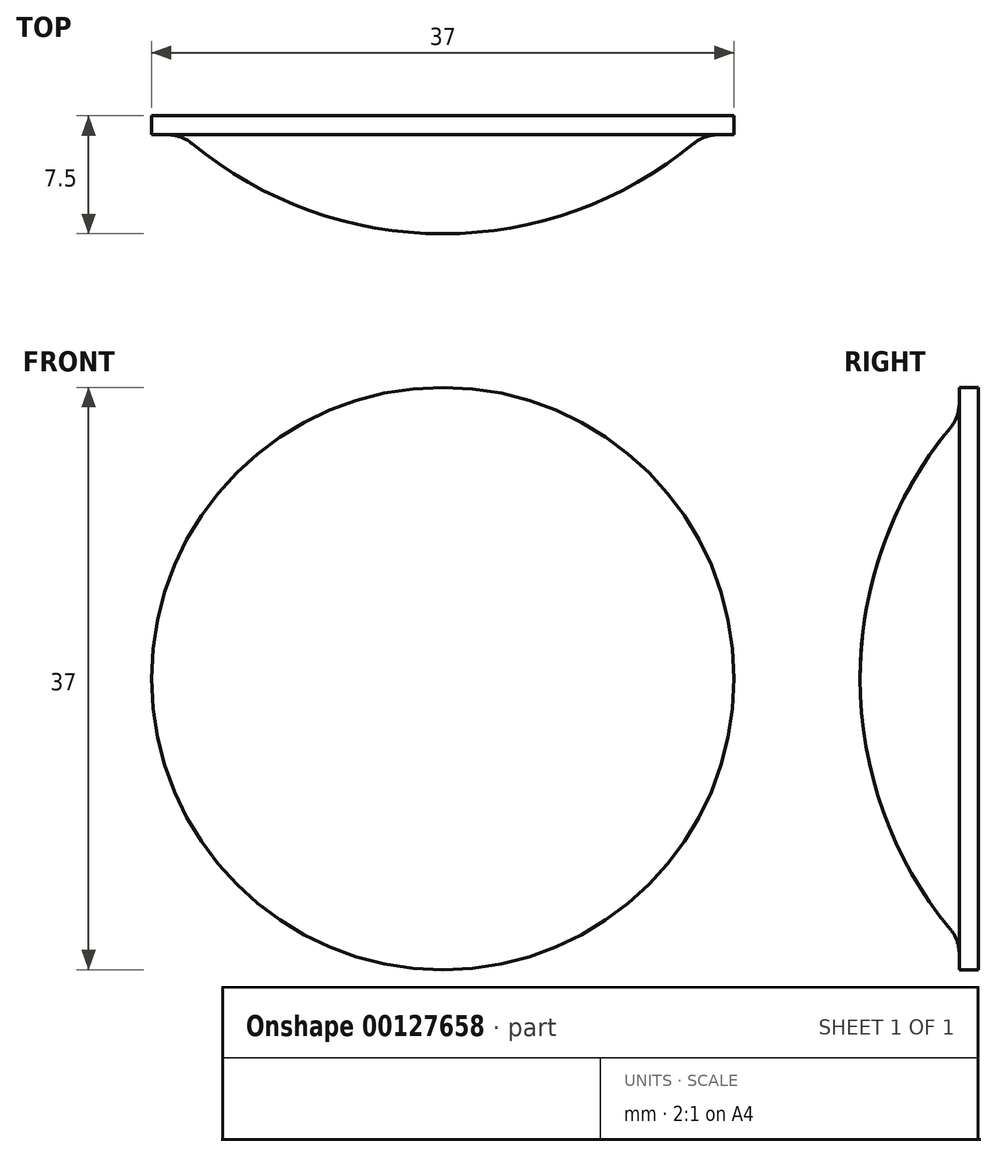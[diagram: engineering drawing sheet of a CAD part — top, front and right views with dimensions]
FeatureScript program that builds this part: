
annotation { "Feature Type Name" : "Feature", "Feature Type Description" : "" }
export const myFeature = defineFeature(function(context is Context, id is Id, definition is map)
    precondition{}
    {
        {
            var Q0;
            Q0=qCreatedBy(makeId("Right.planeOp"),FACE);
            var sketch = newSketch(context, id + "F0", { "sketchPlane" : qUnion([Q0])});
            skLineSegment(sketch, "E0", {"start": v(0, 25) * mm, "end": v(0, -25) * mm, "construction": true});
            skLineSegment(sketch, "E1", {"start": v(0.2, 0) * mm, "end": v(-7.3, 0) * mm});
            skArc(sketch, "E2", {"start": v(-1.57, 15.92) * mm, "mid": v(-5.82, 8.46) * mm, "end": v(-7.3, 0) * mm});
            skArc(sketch, "E3", {"start": v(-1.57, 15.92) * mm, "mid": v(-1.15, 16.67) * mm, "end": v(-1, 17.52) * mm});
            skLineSegment(sketch, "E4", {"start": v(-1, 17.52) * mm, "end": v(-1, 18.5) * mm});
            skLineSegment(sketch, "E5", {"start": v(-1, 18.5) * mm, "end": v(0.2, 18.5) * mm});
            skLineSegment(sketch, "E6", {"start": v(0.2, 18.5) * mm, "end": v(0.2, 0) * mm});
            skLineSegment(sketch, "E7", {"start": v(-7.3, 0) * mm, "end": v(-7.3, -2.7) * mm, "construction": true});
            skSolve(sketch);
        }
        {
            var Q0;
            Q0 = qSketchRegion(id + "F0", true);
            var Q1;
            Q1=makeQuery(id+"F0.imprint","IMPRINT",FACE,{"disambiguationData":[TD([[makeQuery(id+"F0.imprint","IMPRINT",EDGE,{"derivedFrom":sQuery(id+"F0.wireOp",EDGE,"E1")}),-1.0]])]});
            var Q2;
            Q2=sQuery(id+"F0.wireOp",EDGE,"E1");
            revolve(context, id + "F1", {"entities" : qUnion([Q0, Q1]), "axis" : qUnion([Q2]), "revolveType" : RevolveType.FULL});
        }
    });
